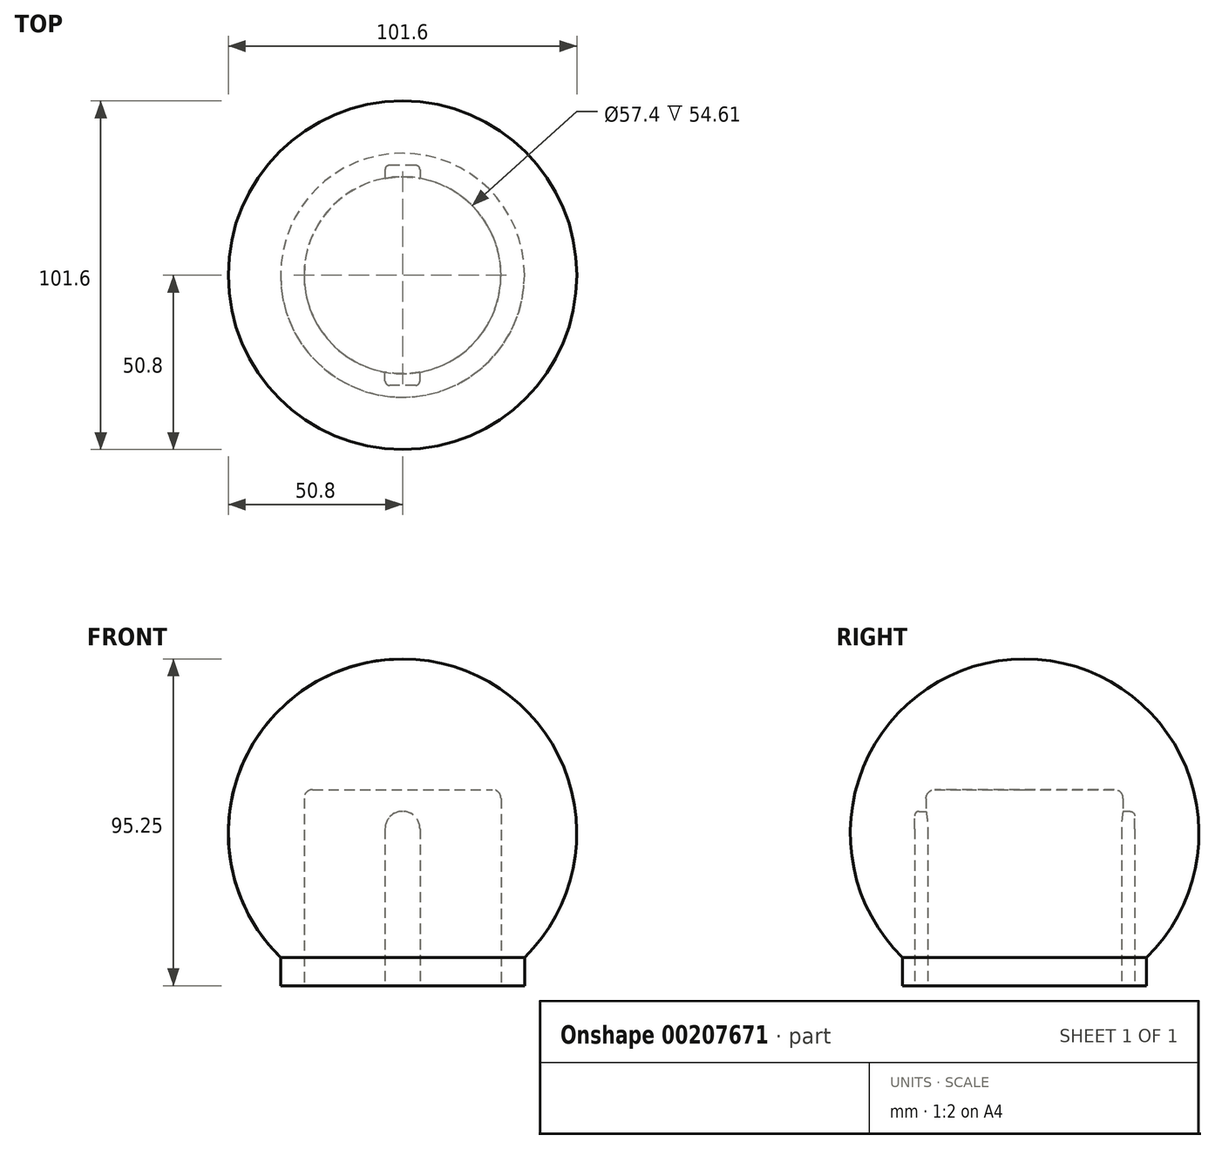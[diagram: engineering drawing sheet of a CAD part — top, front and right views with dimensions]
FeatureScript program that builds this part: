
annotation { "Feature Type Name" : "Feature", "Feature Type Description" : "" }
export const myFeature = defineFeature(function(context is Context, id is Id, definition is map)
    precondition{}
    {
        {
            var Q0;
            Q0=qCreatedBy(makeId("Front.planeOp"),FACE);
            var sketch = newSketch(context, id + "F0", { "sketchPlane" : qUnion([Q0])});
            skArc(sketch, "E0", {"start": v(0, -50.8) * mm, "mid": v(50.8, 0) * mm, "end": v(0, 50.8) * mm});
            skLineSegment(sketch, "E1", {"start": v(0, 0) * mm, "end": v(0, 50.8) * mm});
            skLineSegment(sketch, "E2", {"start": v(0, 0) * mm, "end": v(0, -50.8) * mm});
            skSolve(sketch);
        }
        {
            var Q0;
            Q0=makeQuery(id+"F0.imprint","IMPRINT",FACE,{"disambiguationData":[TD([[makeQuery(id+"F0.imprint","IMPRINT",EDGE,{"derivedFrom":sQuery(id+"F0.wireOp",EDGE,"E0")}),1.0]])]});
            var Q1;
            Q1=sQuery(id+"F0.wireOp",EDGE,"E1");
            revolve(context, id + "F1", {"entities" : qUnion([Q0]), "axis" : qUnion([Q1]), "revolveType" : RevolveType.FULL});
        }
        {
            var Q0;
            Q0=qCreatedBy(makeId("Top.planeOp"),FACE);
            cPlane(context, id + "F2", {"entities" : qUnion([Q0]), "cplaneType" : CPlaneType.OFFSET, "offset" : 44.45 * mm, "oppositeDirection" : true, "width" : 152.4 * mm, "height" : 152.4 * mm});
        }
        {
            var Q0;
            Q0=qCreatedBy(id+"F2.planeOp",FACE);
            var sketch = newSketch(context, id + "F3", { "sketchPlane" : qUnion([Q0])});
            skCircle(sketch, "E3", {"center": v(0, 3.53) * mm, "radius": 128.05 * mm});
            skSolve(sketch);
        }
        {
            var Q0;
            Q0 = qSketchRegion(id + "F3", true);
            extrude(context, id + "F4", {"entities" : qUnion([Q0]), "operationType" : NewBodyOperationType.REMOVE, "oppositeDirection" : true, "depth" : 25.4 * mm});
        }
        {
            var Q0;
            Q0=makeQuery(id+"F4.boolean.opBoolean","COPY",FACE,{"derivedFrom":makeQuery(id+"F4.opExtrude","CAP_FACE",FACE,{"disambiguationData":[OSD([sQuery(id+"F3.wireOp",EDGE,"E3")])],"isStart":true})});
            var sketch = newSketch(context, id + "F5", { "sketchPlane" : qUnion([Q0])});
            skCircle(sketch, "E4", {"center": v(0, 0) * mm, "radius": 35.56 * mm});
            skSolve(sketch);
        }
        {
            var Q0;
            Q0 = qSketchRegion(id + "F5", true);
            extrude(context, id + "F6", {"entities" : qUnion([Q0]), "operationType" : NewBodyOperationType.ADD, "oppositeDirection" : true, "depth" : 25.4 * mm});
        }
        {
            var Q0;
            Q0=makeQuery(id+"F6.boolean.opBoolean","MERGE",FACE,{"derivedFrom":[makeQuery(id+"F4.boolean.opBoolean","COPY",FACE,{"derivedFrom":makeQuery(id+"F4.opExtrude","CAP_FACE",FACE,{"disambiguationData":[OSD([sQuery(id+"F3.wireOp",EDGE,"E3")])],"isStart":true})}),makeQuery(id+"F6.opExtrude","CAP_FACE",FACE,{"disambiguationData":[OSD([sQuery(id+"F5.wireOp",EDGE,"E4")])],"isStart":true})]});
            var sketch = newSketch(context, id + "F7", { "sketchPlane" : qUnion([Q0])});
            skCircle(sketch, "E5", {"center": v(0, 0) * mm, "radius": 28.7 * mm});
            skSolve(sketch);
        }
        {
            var Q0;
            Q0 = qSketchRegion(id + "F7", true);
            extrude(context, id + "F8", {"entities" : qUnion([Q0]), "operationType" : NewBodyOperationType.REMOVE, "oppositeDirection" : true, "depth" : 57.15 * mm});
        }
        {
            var Q0;
            Q0=makeQuery(id+"F6.boolean.opBoolean","MERGE",FACE,{"derivedFrom":[makeQuery(id+"F4.boolean.opBoolean","COPY",FACE,{"derivedFrom":makeQuery(id+"F4.opExtrude","CAP_FACE",FACE,{"disambiguationData":[OSD([sQuery(id+"F3.wireOp",EDGE,"E3")])],"isStart":true})}),makeQuery(id+"F6.opExtrude","CAP_FACE",FACE,{"disambiguationData":[OSD([sQuery(id+"F5.wireOp",EDGE,"E4")])],"isStart":true})]});
            var sketch = newSketch(context, id + "F9", { "sketchPlane" : qUnion([Q0])});
            skLineSegment(sketch, "E6", {"start": v(0, 0) * mm, "end": v(0, 28.7) * mm});
            skCircle(sketch, "E7.0", {"center": v(0, 0) * mm, "radius": 28.7 * mm});
            skLineSegment(sketch, "E8", {"start": v(0, 28.7) * mm, "end": v(0, 32.06) * mm});
            skLineSegment(sketch, "E9", {"start": v(0, 32.06) * mm, "end": v(5.08, 32.06) * mm});
            skLineSegment(sketch, "E10", {"start": v(5.08, 32.06) * mm, "end": v(5.08, 28.25) * mm});
            skLineSegment(sketch, "E11", {"start": v(0, 32.06) * mm, "end": v(-5.08, 32.06) * mm});
            skLineSegment(sketch, "E12", {"start": v(-5.08, 32.06) * mm, "end": v(-5.08, 28.25) * mm});
            skLineSegment(sketch, "E13", {"start": v(0, 0) * mm, "end": v(12.88, 0) * mm});
            skLineSegment(sketch, "E14.MirrorCS", {"start": v(-5.08, -32.06) * mm, "end": v(-5.08, -28.25) * mm});
            skLineSegment(sketch, "E15.MirrorCS", {"start": v(0, -32.06) * mm, "end": v(-5.08, -32.06) * mm});
            skLineSegment(sketch, "E16.MirrorCS", {"start": v(0, -32.06) * mm, "end": v(5.08, -32.06) * mm});
            skLineSegment(sketch, "E17.MirrorCS", {"start": v(5.08, -32.06) * mm, "end": v(5.08, -28.25) * mm});
            skSolve(sketch);
        }
        {
            var Q0;
            {var subQ0=sQuery(id+"F9.wireOp",EDGE,"E8");Q0=makeQuery(id+"F9.imprint","IMPRINT",FACE,{"disambiguationData":[TD([[makeQuery(id+"F9.imprint","IMPRINT",EDGE,{"derivedFrom":subQ0}),1.0]])]});}
            var Q1;
            {var subQ0=sQuery(id+"F9.wireOp",EDGE,"E8");Q1=makeQuery(id+"F9.imprint","IMPRINT",FACE,{"disambiguationData":[TD([[makeQuery(id+"F9.imprint","IMPRINT",EDGE,{"derivedFrom":subQ0}),-1.0]])]});}
            var Q2;
            {var subQ0=sQuery(id+"F9.wireOp",EDGE,"E14.MirrorCS");Q2=makeQuery(id+"F9.imprint","IMPRINT",FACE,{"disambiguationData":[TD([[makeQuery(id+"F9.imprint","IMPRINT",EDGE,{"derivedFrom":subQ0}),-1.0]])]});}
            extrude(context, id + "F10", {"entities" : qUnion([Q0, Q1, Q2]), "operationType" : NewBodyOperationType.REMOVE, "oppositeDirection" : true, "depth" : 50.8 * mm});
        }
        {
            var Q0;
            Q0=makeQuery(id+"F10.boolean.opBoolean","COPY",EDGE,{"derivedFrom":makeQuery(id+"F10.opExtrude","CAP_EDGE",EDGE,{"disambiguationData":[OSD([sQuery(id+"F9.wireOp",EDGE,"E12")])],"isStart":false})});
            var Q1;
            Q1=makeQuery(id+"F10.boolean.opBoolean","COPY",EDGE,{"derivedFrom":makeQuery(id+"F10.opExtrude","CAP_EDGE",EDGE,{"disambiguationData":[OSD([sQuery(id+"F9.wireOp",EDGE,"E10")])],"isStart":false})});
            var Q2;
            Q2=makeQuery(id+"F10.boolean.opBoolean","COPY",EDGE,{"derivedFrom":makeQuery(id+"F10.opExtrude","CAP_EDGE",EDGE,{"disambiguationData":[OSD([sQuery(id+"F9.wireOp",EDGE,"E17.MirrorCS")])],"isStart":false})});
            var Q3;
            Q3=makeQuery(id+"F10.boolean.opBoolean","COPY",EDGE,{"derivedFrom":makeQuery(id+"F10.opExtrude","CAP_EDGE",EDGE,{"disambiguationData":[OSD([sQuery(id+"F9.wireOp",EDGE,"E14.MirrorCS")])],"isStart":false})});
            fillet(context, id + "F11", {"entities" : qUnion([Q0, Q1, Q2, Q3]), "radius" : 5.08 * mm, "tangentPropagation" : true, "allowEdgeOverflow" : false});
        }
        {
            var Q0;
            Q0=makeQuery(id+"F10.boolean.opBoolean","COPY",EDGE,{"derivedFrom":makeQuery(id+"F10.opExtrude","SWEPT_EDGE",EDGE,{"disambiguationData":[OSD([sQuery(id+"F9.wireOp",EDGE,"E7.0"),sQuery(id+"F9.wireOp",EDGE,"E17.MirrorCS")])]})});
            var Q1;
            Q1=makeQuery(id+"F10.boolean.opBoolean","COPY",EDGE,{"derivedFrom":makeQuery(id+"F10.opExtrude","SWEPT_EDGE",EDGE,{"disambiguationData":[OSD([sQuery(id+"F9.wireOp",EDGE,"E16.MirrorCS"),sQuery(id+"F9.wireOp",EDGE,"E17.MirrorCS")])]})});
            var Q2;
            Q2=makeQuery(id+"F10.boolean.opBoolean","COPY",EDGE,{"derivedFrom":makeQuery(id+"F10.opExtrude","SWEPT_EDGE",EDGE,{"disambiguationData":[OSD([sQuery(id+"F9.wireOp",EDGE,"E9"),sQuery(id+"F9.wireOp",EDGE,"E10")])]})});
            var Q3;
            Q3=makeQuery(id+"F10.boolean.opBoolean","COPY",EDGE,{"derivedFrom":makeQuery(id+"F10.opExtrude","SWEPT_EDGE",EDGE,{"disambiguationData":[OSD([sQuery(id+"F9.wireOp",EDGE,"E7.0"),sQuery(id+"F9.wireOp",EDGE,"E10")])]})});
            fillet(context, id + "F12", {"entities" : qUnion([Q0, Q1, Q2, Q3]), "radius" : 1.27 * mm, "tangentPropagation" : true, "allowEdgeOverflow" : false});
        }
        {
            var Q0;
            Q0=makeQuery(id+"F8.boolean.opBoolean","COPY",EDGE,{"derivedFrom":makeQuery(id+"F8.opExtrude","CAP_EDGE",EDGE,{"disambiguationData":[OSD([sQuery(id+"F7.wireOp",EDGE,"E5")])],"isStart":false})});
            fillet(context, id + "F13", {"entities" : qUnion([Q0]), "radius" : 2.54 * mm, "tangentPropagation" : true, "allowEdgeOverflow" : false});
        }
    });
